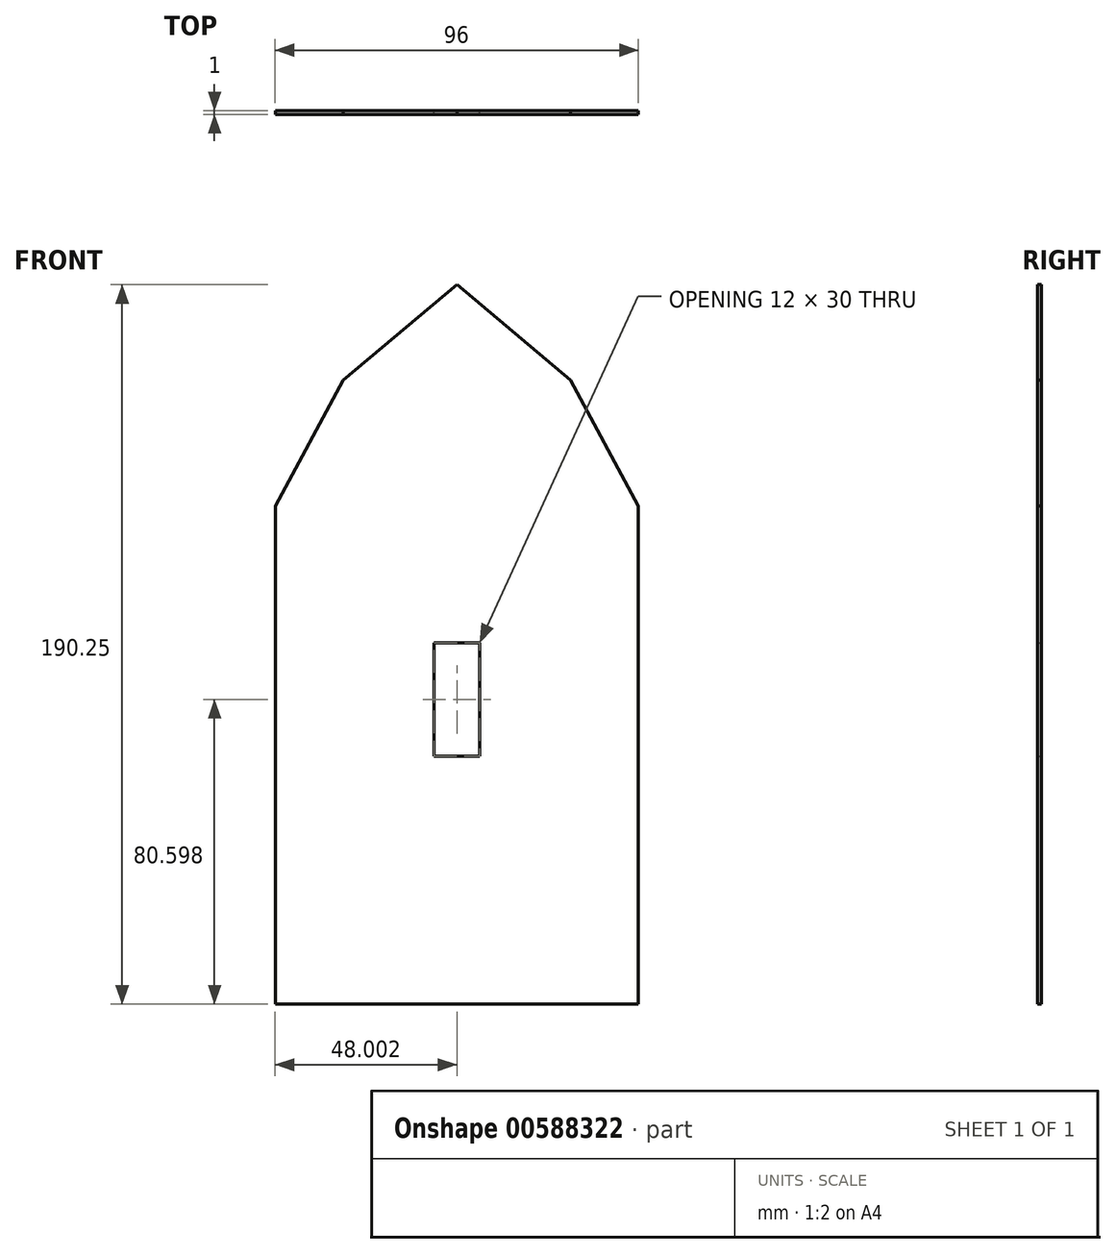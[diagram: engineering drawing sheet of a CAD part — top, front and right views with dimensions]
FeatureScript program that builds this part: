
annotation { "Feature Type Name" : "Feature", "Feature Type Description" : "" }
export const myFeature = defineFeature(function(context is Context, id is Id, definition is map)
    precondition{}
    {
        {
            var Q0;
            Q0=qCreatedBy(makeId("Front.planeOp"),FACE);
            var sketch = newSketch(context, id + "F0", { "sketchPlane" : qUnion([Q0])});
            skLineSegment(sketch, "E0", {"start": v(163.7, -53.31) * mm, "end": v(163.7, -20.56) * mm});
            skLineSegment(sketch, "E1", {"start": v(163.7, -20.56) * mm, "end": v(163.7, 52.44) * mm});
            skLineSegment(sketch, "E2", {"start": v(163.7, 52.44) * mm, "end": v(163.7, 55.64) * mm});
            skLineSegment(sketch, "E3", {"start": v(121.7, 55.64) * mm, "end": v(109.7, 55.64) * mm});
            skLineSegment(sketch, "E4", {"start": v(163.7, -53.31) * mm, "end": v(115.7, -53.31) * mm});
            skLineSegment(sketch, "E5", {"start": v(67.7, -53.31) * mm, "end": v(67.7, 55.64) * mm});
            skLineSegment(sketch, "E6", {"start": v(115.7, 55.64) * mm, "end": v(121.7, 55.64) * mm});
            skLineSegment(sketch, "E7", {"start": v(109.7, 55.64) * mm, "end": v(121.7, 55.64) * mm});
            skPoint(sketch, "E8.trimOffspring.end.orphan", {"position": v(115.7, -53.31) * mm});
            skLineSegment(sketch, "E9", {"start": v(145.7, 88.94) * mm, "end": v(163.7, 55.64) * mm});
            skLineSegment(sketch, "E10", {"start": v(115.7, 114.19) * mm, "end": v(145.7, 88.94) * mm});
            skLineSegment(sketch, "E11", {"start": v(121.2, 88.94) * mm, "end": v(110.2, 88.94) * mm});
            skLineSegment(sketch, "E12", {"start": v(115.7, 114.19) * mm, "end": v(85.7, 88.94) * mm});
            skLineSegment(sketch, "E13", {"start": v(67.7, 55.64) * mm, "end": v(85.7, 88.94) * mm});
            skLineSegment(sketch, "E14", {"start": v(115.7, 88.94) * mm, "end": v(110.2, 88.94) * mm});
            skLineSegment(sketch, "E15", {"start": v(110.2, 100.94) * mm, "end": v(121.2, 100.94) * mm});
            skLineSegment(sketch, "E16", {"start": v(121.2, 88.94) * mm, "end": v(115.7, 88.94) * mm});
            skLineSegment(sketch, "E17", {"start": v(115.7, 114.19) * mm, "end": v(115.7, 55.64) * mm});
            skLineSegment(sketch, "E18", {"start": v(67.7, -53.31) * mm, "end": v(67.7, -76.06) * mm});
            skLineSegment(sketch, "E19", {"start": v(67.7, -76.06) * mm, "end": v(163.7, -76.06) * mm});
            skLineSegment(sketch, "E20", {"start": v(163.7, -76.06) * mm, "end": v(163.7, -53.31) * mm});
            skLineSegment(sketch, "E21", {"start": v(109.7, 19.54) * mm, "end": v(121.7, 19.54) * mm});
            skLineSegment(sketch, "E22", {"start": v(121.7, 19.54) * mm, "end": v(121.7, -8.46) * mm});
            skLineSegment(sketch, "E23", {"start": v(109.7, -8.46) * mm, "end": v(109.7, 19.54) * mm});
            skLineSegment(sketch, "E24", {"start": v(109.7, 42.64) * mm, "end": v(121.7, 42.64) * mm});
            skLineSegment(sketch, "E25", {"start": v(121.7, -8.46) * mm, "end": v(121.7, -9.46) * mm});
            skLineSegment(sketch, "E26", {"start": v(109.7, -8.46) * mm, "end": v(109.7, -9.46) * mm});
            skLineSegment(sketch, "E27", {"start": v(121.7, -9.46) * mm, "end": v(121.7, -10.46) * mm});
            skLineSegment(sketch, "E28", {"start": v(121.7, -10.46) * mm, "end": v(107.48, -10.46) * mm});
            skLineSegment(sketch, "E29", {"start": v(109.7, -9.46) * mm, "end": v(109.7, -10.46) * mm});
            skSolve(sketch);
        }
        {
            var Q0;
            Q0=makeQuery(id+"F0.imprint","IMPRINT",FACE,{"disambiguationData":[TD([[makeQuery(id+"F0.imprint","IMPRINT",EDGE,{"derivedFrom":sQuery(id+"F0.wireOp",EDGE,"E0")}),1.0]])]});
            extrude(context, id + "F1", {"entities" : qUnion([Q0]), "depth" : 1 * mm, "offsetDistance" : 25 * mm});
        }
    });
